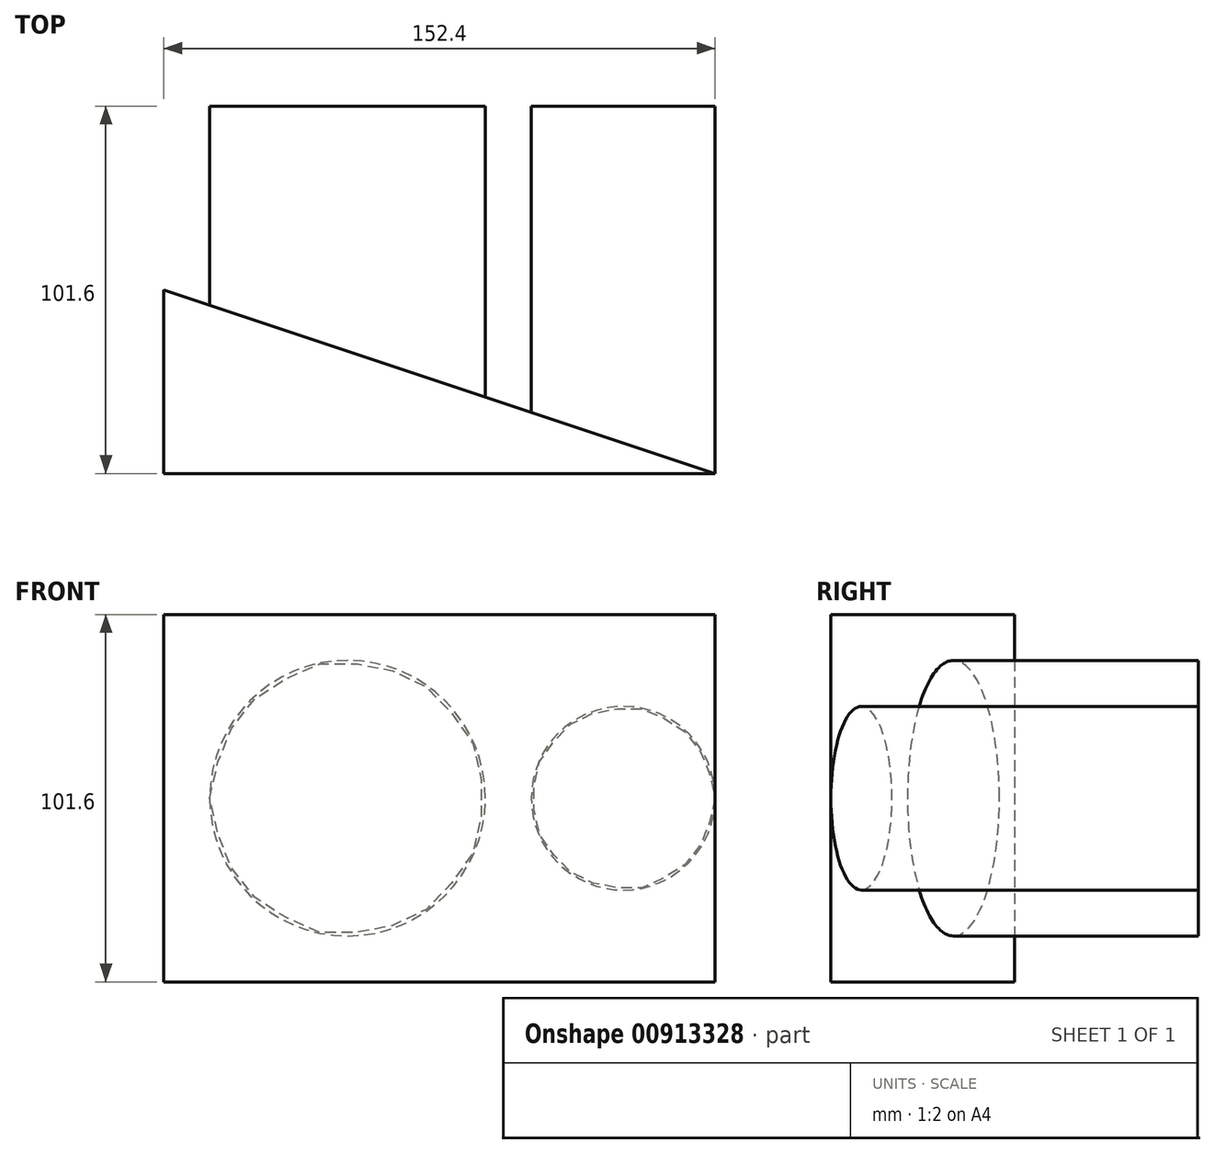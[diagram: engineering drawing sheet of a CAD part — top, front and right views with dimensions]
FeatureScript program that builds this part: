
annotation { "Feature Type Name" : "Feature", "Feature Type Description" : "" }
export const myFeature = defineFeature(function(context is Context, id is Id, definition is map)
    precondition{}
    {
        {
            var Q0;
            Q0=qCreatedBy(makeId("Top.planeOp"),FACE);
            var sketch = newSketch(context, id + "F0", { "sketchPlane" : qUnion([Q0])});
            skLineSegment(sketch, "E0.bottom", {"start": v(0, 0) * mm, "end": v(152.4, 0) * mm});
            skLineSegment(sketch, "E0.top", {"start": v(0, -50.8) * mm, "end": v(152.4, -50.8) * mm});
            skLineSegment(sketch, "E0.left", {"start": v(0, 0) * mm, "end": v(0, -50.8) * mm});
            skLineSegment(sketch, "E0.right", {"start": v(152.4, 0) * mm, "end": v(152.4, -50.8) * mm});
            skLineSegment(sketch, "E1", {"start": v(0, 0) * mm, "end": v(152.4, -50.8) * mm});
            skSolve(sketch);
        }
        {
            var Q0;
            Q0=makeQuery(id+"F0.imprint","IMPRINT",FACE,{"disambiguationData":[TD([[makeQuery(id+"F0.imprint","IMPRINT",EDGE,{"derivedFrom":sQuery(id+"F0.wireOp",EDGE,"E0.top")}),1.0]])]});
            extrude(context, id + "F1", {"entities" : qUnion([Q0]), "depth" : 101.6 * mm, "offsetDistance" : 25.4 * mm});
        }
        {
            var Q0;
            Q0=qCreatedBy(makeId("Front.planeOp"),FACE);
            cPlane(context, id + "F2", {"entities" : qUnion([Q0]), "cplaneType" : CPlaneType.OFFSET, "offset" : 50.8 * mm, "oppositeDirection" : true, "width" : 152.4 * mm, "height" : 152.4 * mm});
        }
        {
            var Q0;
            Q0=qCreatedBy(id+"F2.planeOp",FACE);
            var sketch = newSketch(context, id + "F3", { "sketchPlane" : qUnion([Q0])});
            skLineSegment(sketch, "E2.bottom", {"start": v(0, 0) * mm, "end": v(50.8, 0) * mm, "construction": true});
            skLineSegment(sketch, "E2.top", {"start": v(0, 50.8) * mm, "end": v(50.8, 50.8) * mm, "construction": true});
            skLineSegment(sketch, "E2.left", {"start": v(0, 0) * mm, "end": v(0, 50.8) * mm, "construction": true});
            skLineSegment(sketch, "E2.right", {"start": v(50.8, 0) * mm, "end": v(50.8, 50.8) * mm, "construction": true});
            skCircle(sketch, "E3", {"center": v(50.8, 50.8) * mm, "radius": 38.1 * mm});
            skLineSegment(sketch, "E4.bottom", {"start": v(0, 0) * mm, "end": v(127, 0) * mm, "construction": true});
            skLineSegment(sketch, "E4.top", {"start": v(0, 50.8) * mm, "end": v(127, 50.8) * mm, "construction": true});
            skLineSegment(sketch, "E4.right", {"start": v(127, 0) * mm, "end": v(127, 50.8) * mm, "construction": true});
            skCircle(sketch, "E5", {"center": v(127, 50.8) * mm, "radius": 25.4 * mm});
            skSolve(sketch);
        }
        {
            var Q0;
            Q0 = qSketchRegion(id + "F3", true);
            var Q1;
            Q1 = qConstructionFilter(qBodyType(qCreatedBy(id + "F3" ,EDGE), BodyType.WIRE), ConstructionObject.NO);
            var Q2;
            Q2=makeQuery(id+"F1.opExtrude","SWEPT_FACE",FACE,{"disambiguationData":[OSD([sQuery(id+"F0.wireOp",EDGE,"E0.top")])]});
            extrude(context, id + "F4", {"entities" : qUnion([Q0]), "operationType" : NewBodyOperationType.ADD, "surfaceEntities" : qUnion([Q1]), "endBound" : BoundingType.UP_TO_SURFACE, "depth" : 25.4 * mm, "endBoundEntityFace" : qUnion([Q2]), "offsetDistance" : 25.4 * mm});
        }
    });
